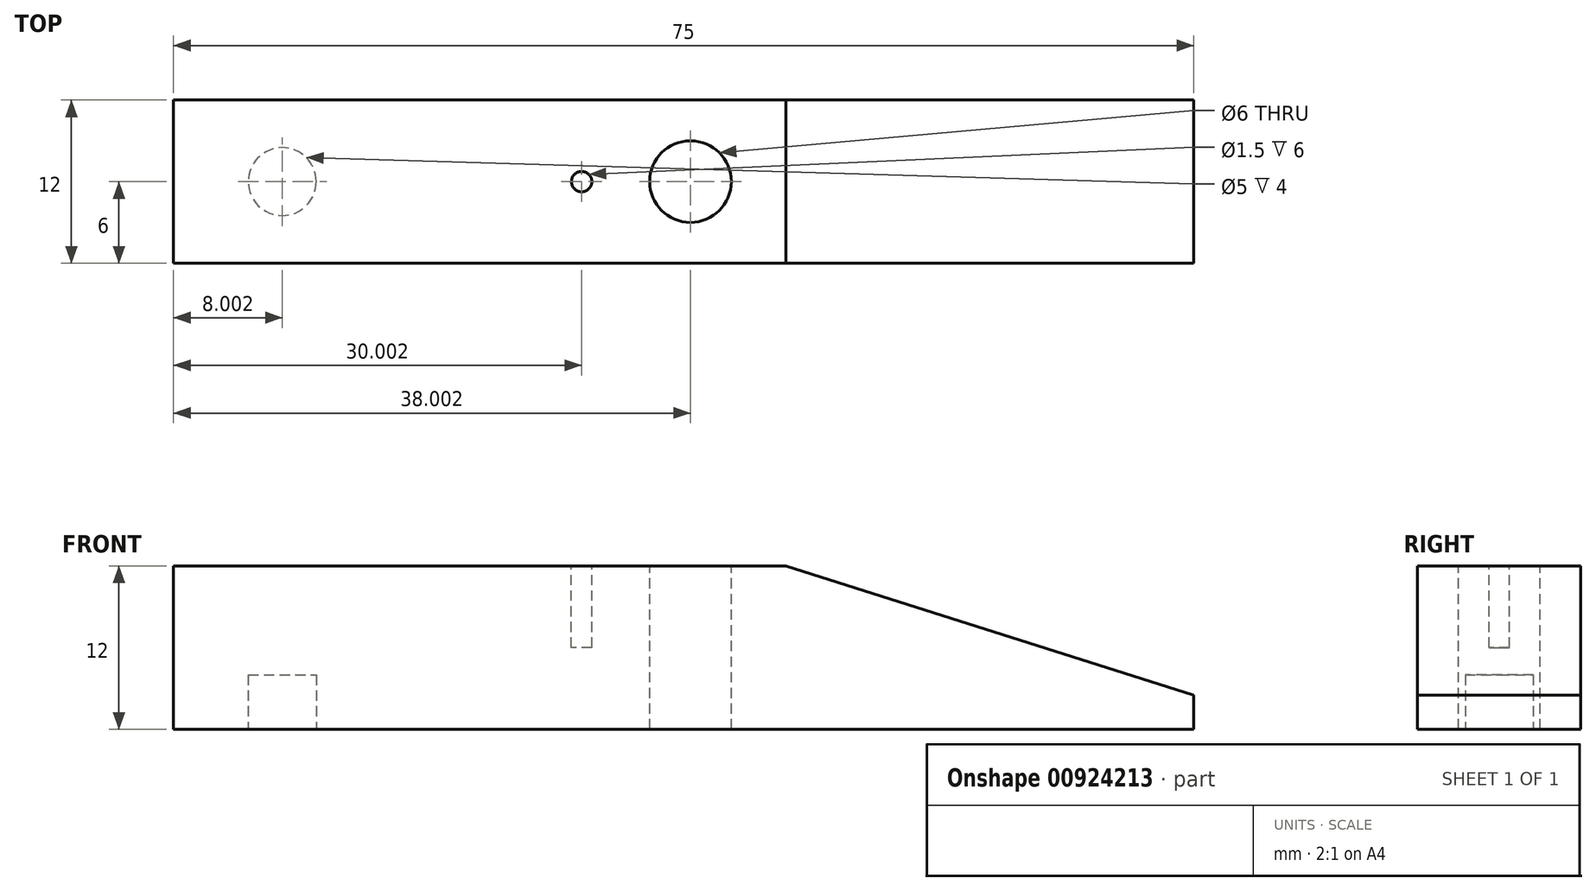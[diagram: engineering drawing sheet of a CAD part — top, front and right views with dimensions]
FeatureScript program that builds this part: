
annotation { "Feature Type Name" : "Feature", "Feature Type Description" : "" }
export const myFeature = defineFeature(function(context is Context, id is Id, definition is map)
    precondition{}
    {
        {
            var Q0;
            Q0=qCreatedBy(makeId("Front.planeOp"),FACE);
            var sketch = newSketch(context, id + "F0", { "sketchPlane" : qUnion([Q0])});
            skLineSegment(sketch, "E0", {"start": v(-11.5, 16.7) * mm, "end": v(33.5, 16.7) * mm});
            skLineSegment(sketch, "E1", {"start": v(33.5, 16.7) * mm, "end": v(63.5, 7.2) * mm});
            skLineSegment(sketch, "E2", {"start": v(63.5, 7.2) * mm, "end": v(63.5, 4.7) * mm});
            skLineSegment(sketch, "E3", {"start": v(63.5, 4.7) * mm, "end": v(-11.5, 4.7) * mm});
            skLineSegment(sketch, "E4", {"start": v(-11.5, 4.7) * mm, "end": v(-11.5, 16.7) * mm});
            skSolve(sketch);
        }
        {
            var Q0;
            Q0=makeQuery(id+"F0.imprint","IMPRINT",FACE,{"disambiguationData":[TD([[makeQuery(id+"F0.imprint","IMPRINT",EDGE,{"derivedFrom":sQuery(id+"F0.wireOp",EDGE,"E0")}),-1.0]])]});
            extrude(context, id + "F1", {"entities" : qUnion([Q0]), "depth" : 12 * mm, "offsetDistance" : 25 * mm});
        }
        {
            var Q0;
            Q0=makeQuery(id+"F1.opExtrude","SWEPT_FACE",FACE,{"disambiguationData":[OSD([sQuery(id+"F0.wireOp",EDGE,"E0")])]});
            var sketch = newSketch(context, id + "F2", { "sketchPlane" : qUnion([Q0])});
            skLineSegment(sketch, "E5", {"start": v(-11.5, 0) * mm, "end": v(-11.5, -6) * mm});
            skCircle(sketch, "E6", {"center": v(26.5, -6) * mm, "radius": 3 * mm});
            skSolve(sketch);
        }
        {
            var Q0;
            Q0=makeQuery(id+"F2.imprint","IMPRINT",FACE,{"disambiguationData":[TD([[makeQuery(id+"F2.imprint","IMPRINT",EDGE,{"derivedFrom":sQuery(id+"F2.wireOp",EDGE,"E6")}),1.0]])]});
            extrude(context, id + "F3", {"entities" : qUnion([Q0]), "operationType" : NewBodyOperationType.REMOVE, "oppositeDirection" : true, "depth" : 25 * mm, "offsetDistance" : 25 * mm});
        }
        {
            var Q0;
            Q0=makeQuery(id+"F1.opExtrude","SWEPT_FACE",FACE,{"disambiguationData":[OSD([sQuery(id+"F0.wireOp",EDGE,"E0")])]});
            var sketch = newSketch(context, id + "F4", { "sketchPlane" : qUnion([Q0])});
            skCircle(sketch, "E7", {"center": v(18.5, -6) * mm, "radius": 0.75 * mm});
            skSolve(sketch);
        }
        {
            var Q0;
            Q0=makeQuery(id+"F4.imprint","IMPRINT",FACE,{"disambiguationData":[TD([[makeQuery(id+"F4.imprint","IMPRINT",EDGE,{"derivedFrom":sQuery(id+"F4.wireOp",EDGE,"E7")}),1.0]])]});
            extrude(context, id + "F5", {"entities" : qUnion([Q0]), "operationType" : NewBodyOperationType.REMOVE, "oppositeDirection" : true, "depth" : 6 * mm, "offsetDistance" : 25 * mm});
        }
        {
            var Q0;
            Q0=makeQuery(id+"F1.opExtrude","SWEPT_FACE",FACE,{"disambiguationData":[OSD([sQuery(id+"F0.wireOp",EDGE,"E3")])]});
            var sketch = newSketch(context, id + "F6", { "sketchPlane" : qUnion([Q0])});
            skCircle(sketch, "E8", {"center": v(-3.5, 6) * mm, "radius": 2.5 * mm});
            skSolve(sketch);
        }
        {
            var Q0;
            Q0 = qSketchRegion(id + "F6", true);
            extrude(context, id + "F7", {"entities" : qUnion([Q0]), "operationType" : NewBodyOperationType.REMOVE, "oppositeDirection" : true, "depth" : 4 * mm, "offsetDistance" : 25 * mm});
        }
    });
